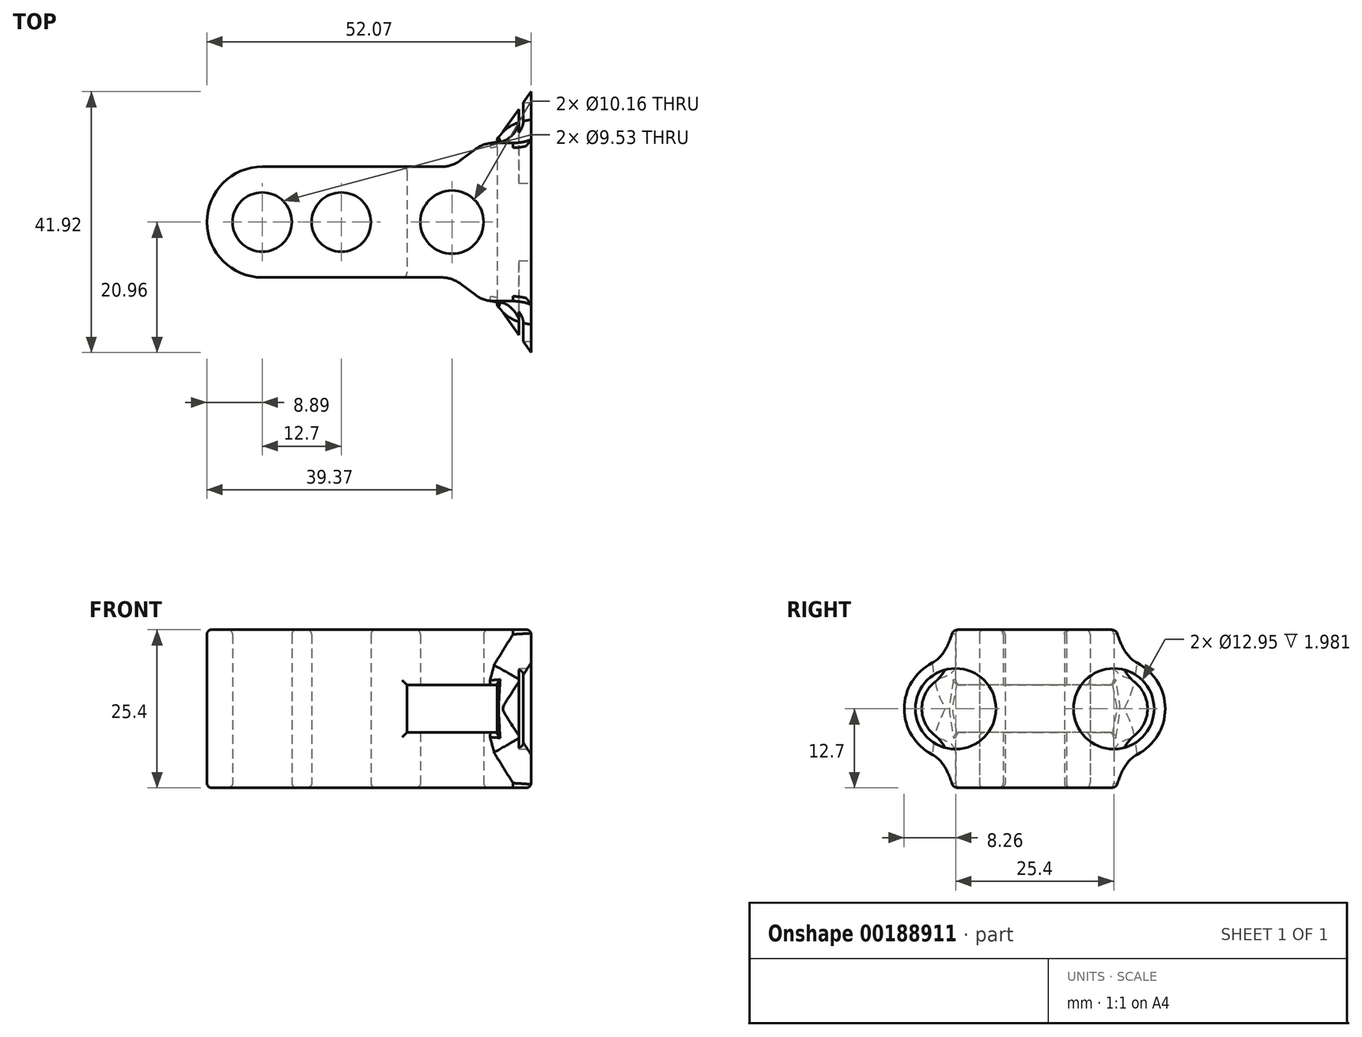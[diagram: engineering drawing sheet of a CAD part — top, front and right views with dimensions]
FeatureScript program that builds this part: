
annotation { "Feature Type Name" : "Feature", "Feature Type Description" : "" }
export const myFeature = defineFeature(function(context is Context, id is Id, definition is map)
    precondition{}
    {
        {
            var Q0;
            Q0=qCreatedBy(makeId("Top.planeOp"),FACE);
            var sketch = newSketch(context, id + "F0", { "sketchPlane" : qUnion([Q0])});
            skCircle(sketch, "E0", {"center": v(-12.7, 0) * mm, "radius": 4.76 * mm});
            skCircle(sketch, "E1", {"center": v(0, 0) * mm, "radius": 4.76 * mm});
            skCircle(sketch, "E2", {"center": v(17.78, 0) * mm, "radius": 5.08 * mm});
            skArc(sketch, "E3", {"start": v(-12.7, 8.9) * mm, "mid": v(-21.59, 0) * mm, "end": v(-12.7, -8.9) * mm});
            skLineSegment(sketch, "E4", {"start": v(-12.7, 8.9) * mm, "end": v(17.78, 8.9) * mm});
            skLineSegment(sketch, "E5", {"start": v(-12.7, 0) * mm, "end": v(-12.7, 8.9) * mm, "construction": true});
            skLineSegment(sketch, "E6", {"start": v(17.78, 0) * mm, "end": v(17.78, 8.9) * mm, "construction": true});
            skLineSegment(sketch, "E7", {"start": v(-12.7, -8.9) * mm, "end": v(17.78, -8.9) * mm});
            skLineSegment(sketch, "E8", {"start": v(30.48, 12.7) * mm, "end": v(30.48, -12.7) * mm});
            skLineSegment(sketch, "E9", {"start": v(30.48, -12.7) * mm, "end": v(22.86, -12.7) * mm});
            skLineSegment(sketch, "E10", {"start": v(22.86, -12.7) * mm, "end": v(17.78, -8.9) * mm});
            skLineSegment(sketch, "E11", {"start": v(30.48, 12.7) * mm, "end": v(22.86, 12.7) * mm});
            skLineSegment(sketch, "E12", {"start": v(22.86, 12.7) * mm, "end": v(17.78, 8.9) * mm});
            skLineSegment(sketch, "E13", {"start": v(17.78, 0) * mm, "end": v(30.48, 0) * mm, "construction": true});
            skLineSegment(sketch, "E14", {"start": v(17.78, 0) * mm, "end": v(17.78, -8.9) * mm, "construction": true});
            skSolve(sketch);
        }
        {
            var Q0;
            Q0=qSketchRegion(id+"F0",true);
            extrude(context, id + "F1", {"entities" : qUnion([Q0]), "depth" : 25.4 * mm});
        }
        {
            var Q0;
            Q0=qCreatedBy(makeId("Front.planeOp"),FACE);
            var sketch = newSketch(context, id + "F2", { "sketchPlane" : qUnion([Q0])});
            skLineSegment(sketch, "E15.bottom", {"start": v(10.54, 8.9) * mm, "end": v(25.02, 8.9) * mm});
            skLineSegment(sketch, "E15.top", {"start": v(10.54, 16.51) * mm, "end": v(25.02, 16.51) * mm});
            skLineSegment(sketch, "E15.left", {"start": v(10.54, 8.9) * mm, "end": v(10.54, 16.51) * mm});
            skLineSegment(sketch, "E15.right", {"start": v(25.02, 8.9) * mm, "end": v(25.02, 16.51) * mm});
            skLineSegment(sketch, "E16", {"start": v(10.54, 12.7) * mm, "end": v(0, 12.7) * mm, "construction": true});
            skLineSegment(sketch, "E17", {"start": v(17.78, 16.51) * mm, "end": v(17.78, 25.4) * mm, "construction": true});
            skSolve(sketch);
        }
        {
            var Q0;
            Q0=qSketchRegion(id+"F2",true);
            extrude(context, id + "F3", {"entities" : qUnion([Q0]), "operationType" : NewBodyOperationType.REMOVE, "endBound" : BoundingType.SYMMETRIC, "oppositeDirection" : true, "depth" : 25.4 * mm});
        }
        {
            var Q0;
            Q0=makeQuery(id+"F1.opExtrude","SWEPT_FACE",FACE,{"disambiguationData":[OSD([sQuery(id+"F0.wireOp",EDGE,"E8")])]});
            var sketch = newSketch(context, id + "F4", { "sketchPlane" : qUnion([Q0])});
            skCircle(sketch, "E18", {"center": v(-12.7, 12.7) * mm, "radius": 8.26 * mm});
            skCircle(sketch, "E19", {"center": v(12.7, 12.7) * mm, "radius": 8.26 * mm});
            skLineSegment(sketch, "E20", {"start": v(-12.7, 12.7) * mm, "end": v(0, 0) * mm, "construction": true});
            skLineSegment(sketch, "E21", {"start": v(0, 0) * mm, "end": v(12.7, 12.7) * mm, "construction": true});
            skLineSegment(sketch, "E22", {"start": v(-12.7, 12.7) * mm, "end": v(12.7, 12.7) * mm, "construction": true});
            skSolve(sketch);
        }
        {
            var Q0;
            Q0=qSketchRegion(id+"F4",true);
            extrude(context, id + "F5", {"entities" : qUnion([Q0]), "operationType" : NewBodyOperationType.ADD, "oppositeDirection" : true, "depth" : 5.46 * mm, "hasDraft" : true, "draftAngle" : 55 * degree, "draftPullDirection" : true});
        }
        {
            var Q0;
            {var subQ0=sQuery(id+"F0.wireOp",EDGE,"E12");var subQ1=sQuery(id+"F0.wireOp",EDGE,"E11");Q0=makeQuery(id+"F3.boolean.opBoolean","SPLIT",EDGE,{"disambiguationData":[TD([makeQuery(id+"F3.opExtrude","SWEPT_FACE",FACE,{"disambiguationData":[OSD([sQuery(id+"F2.wireOp",EDGE,"E15.bottom")])]})])],"derivedFrom":makeQuery(id+"F1.opExtrude","SWEPT_EDGE",EDGE,{"disambiguationData":[OSD([subQ1,subQ0])]})});}
            var Q1;
            {var subQ0=sQuery(id+"F0.wireOp",EDGE,"E12");var subQ1=sQuery(id+"F0.wireOp",EDGE,"E4");Q1=makeQuery(id+"F3.boolean.opBoolean","SPLIT",EDGE,{"disambiguationData":[TD([makeQuery(id+"F3.opExtrude","SWEPT_FACE",FACE,{"disambiguationData":[OSD([sQuery(id+"F2.wireOp",EDGE,"E15.bottom")])]})])],"derivedFrom":makeQuery(id+"F1.opExtrude","SWEPT_EDGE",EDGE,{"disambiguationData":[OSD([subQ1,subQ0])]})});}
            var Q2;
            {var subQ0=sQuery(id+"F0.wireOp",EDGE,"E12");var subQ1=sQuery(id+"F0.wireOp",EDGE,"E4");Q2=makeQuery(id+"F3.boolean.opBoolean","SPLIT",EDGE,{"disambiguationData":[TD([makeQuery(id+"F3.opExtrude","SWEPT_FACE",FACE,{"disambiguationData":[OSD([sQuery(id+"F2.wireOp",EDGE,"E15.top")])]})])],"derivedFrom":makeQuery(id+"F1.opExtrude","SWEPT_EDGE",EDGE,{"disambiguationData":[OSD([subQ1,subQ0])]})});}
            var Q3;
            {var subQ0=sQuery(id+"F0.wireOp",EDGE,"E12");var subQ1=sQuery(id+"F0.wireOp",EDGE,"E11");Q3=makeQuery(id+"F3.boolean.opBoolean","SPLIT",EDGE,{"disambiguationData":[TD([makeQuery(id+"F3.opExtrude","SWEPT_FACE",FACE,{"disambiguationData":[OSD([sQuery(id+"F2.wireOp",EDGE,"E15.top")])]})])],"derivedFrom":makeQuery(id+"F1.opExtrude","SWEPT_EDGE",EDGE,{"disambiguationData":[OSD([subQ1,subQ0])]})});}
            var Q4;
            {var subQ0=sQuery(id+"F0.wireOp",EDGE,"E10");var subQ1=sQuery(id+"F0.wireOp",EDGE,"E7");Q4=makeQuery(id+"F3.boolean.opBoolean","SPLIT",EDGE,{"disambiguationData":[TD([makeQuery(id+"F3.opExtrude","SWEPT_FACE",FACE,{"disambiguationData":[OSD([sQuery(id+"F2.wireOp",EDGE,"E15.top")])]})])],"derivedFrom":makeQuery(id+"F1.opExtrude","SWEPT_EDGE",EDGE,{"disambiguationData":[OSD([subQ1,subQ0])]})});}
            var Q5;
            {var subQ0=sQuery(id+"F0.wireOp",EDGE,"E10");var subQ1=sQuery(id+"F0.wireOp",EDGE,"E9");Q5=makeQuery(id+"F3.boolean.opBoolean","SPLIT",EDGE,{"disambiguationData":[TD([makeQuery(id+"F3.opExtrude","SWEPT_FACE",FACE,{"disambiguationData":[OSD([sQuery(id+"F2.wireOp",EDGE,"E15.top")])]})])],"derivedFrom":makeQuery(id+"F1.opExtrude","SWEPT_EDGE",EDGE,{"disambiguationData":[OSD([subQ1,subQ0])]})});}
            var Q6;
            {var subQ0=sQuery(id+"F0.wireOp",EDGE,"E10");var subQ1=sQuery(id+"F0.wireOp",EDGE,"E7");Q6=makeQuery(id+"F3.boolean.opBoolean","SPLIT",EDGE,{"disambiguationData":[TD([makeQuery(id+"F3.opExtrude","SWEPT_FACE",FACE,{"disambiguationData":[OSD([sQuery(id+"F2.wireOp",EDGE,"E15.bottom")])]})])],"derivedFrom":makeQuery(id+"F1.opExtrude","SWEPT_EDGE",EDGE,{"disambiguationData":[OSD([subQ1,subQ0])]})});}
            var Q7;
            {var subQ0=sQuery(id+"F0.wireOp",EDGE,"E10");var subQ1=sQuery(id+"F0.wireOp",EDGE,"E9");Q7=makeQuery(id+"F3.boolean.opBoolean","SPLIT",EDGE,{"disambiguationData":[TD([makeQuery(id+"F3.opExtrude","SWEPT_FACE",FACE,{"disambiguationData":[OSD([sQuery(id+"F2.wireOp",EDGE,"E15.bottom")])]})])],"derivedFrom":makeQuery(id+"F1.opExtrude","SWEPT_EDGE",EDGE,{"disambiguationData":[OSD([subQ1,subQ0])]})});}
            fillet(context, id + "F6", {"entities" : qUnion([Q0, Q1, Q2, Q3, Q4, Q5, Q6, Q7]), "radius" : 5.08 * mm, "tangentPropagation" : true, "allowEdgeOverflow" : false});
        }
        {
            var Q0;
            Q0=makeQuery(id+"F5.boolean.opBoolean","INTERSECT",EDGE,{"disambiguationData":[OD(0.0)],"derivedFrom":[makeQuery(id+"F1.opExtrude","SWEPT_FACE",FACE,{"disambiguationData":[OSD([sQuery(id+"F0.wireOp",EDGE,"E9")])]}),makeQuery(id+"F5.opExtrude","SWEPT_FACE",FACE,{"disambiguationData":[OSD([sQuery(id+"F4.wireOp",EDGE,"E18")])]})]});
            var Q1;
            Q1=makeQuery(id+"F5.boolean.opBoolean","INTERSECT",EDGE,{"disambiguationData":[OD(1.0)],"derivedFrom":[makeQuery(id+"F1.opExtrude","SWEPT_FACE",FACE,{"disambiguationData":[OSD([sQuery(id+"F0.wireOp",EDGE,"E9")])]}),makeQuery(id+"F5.opExtrude","SWEPT_FACE",FACE,{"disambiguationData":[OSD([sQuery(id+"F4.wireOp",EDGE,"E18")])]})]});
            var Q2;
            Q2=makeQuery(id+"F5.boolean.opBoolean","INTERSECT",EDGE,{"disambiguationData":[OD(1.0)],"derivedFrom":[makeQuery(id+"F1.opExtrude","SWEPT_FACE",FACE,{"disambiguationData":[OSD([sQuery(id+"F0.wireOp",EDGE,"E11")])]}),makeQuery(id+"F5.opExtrude","SWEPT_FACE",FACE,{"disambiguationData":[OSD([sQuery(id+"F4.wireOp",EDGE,"E19")])]})]});
            var Q3;
            Q3=makeQuery(id+"F5.boolean.opBoolean","INTERSECT",EDGE,{"disambiguationData":[OD(0.0)],"derivedFrom":[makeQuery(id+"F1.opExtrude","SWEPT_FACE",FACE,{"disambiguationData":[OSD([sQuery(id+"F0.wireOp",EDGE,"E11")])]}),makeQuery(id+"F5.opExtrude","SWEPT_FACE",FACE,{"disambiguationData":[OSD([sQuery(id+"F4.wireOp",EDGE,"E19")])]})]});
            fillet(context, id + "F7", {"entities" : qUnion([Q0, Q1, Q2, Q3]), "radius" : 5.08 * mm, "tangentPropagation" : true, "allowEdgeOverflow" : false});
        }
        {
            var Q0;
            {var subQ0=sQuery(id+"F4.wireOp",EDGE,"E18");Q0=makeQuery(id+"F7.opFillet","BLEND_EDGE",EDGE,{"disambiguationData":[OD(1.0)],"blendedFrom":[makeQuery(id+"F5.boolean.opBoolean","INTERSECT",EDGE,{"disambiguationData":[OD(1.0)],"derivedFrom":[makeQuery(id+"F1.opExtrude","SWEPT_FACE",FACE,{"disambiguationData":[OSD([sQuery(id+"F0.wireOp",EDGE,"E9")])]}),makeQuery(id+"F5.opExtrude","SWEPT_FACE",FACE,{"disambiguationData":[OSD([subQ0])]})]}),makeQuery(id+"F5.boolean.opBoolean","MERGE",FACE,{"derivedFrom":[makeQuery(id+"F3.boolean.opBoolean","COPY",FACE,{"derivedFrom":makeQuery(id+"F3.opExtrude","SWEPT_FACE",FACE,{"disambiguationData":[OSD([sQuery(id+"F2.wireOp",EDGE,"E15.right")])]})}),makeQuery(id+"F5.opExtrude","CAP_FACE",FACE,{"disambiguationData":[OSD([subQ0])],"isStart":false}),makeQuery(id+"F5.opExtrude","CAP_FACE",FACE,{"disambiguationData":[OSD([sQuery(id+"F4.wireOp",EDGE,"E19")])],"isStart":false})]})],"blendedInto":[makeQuery(id+"F5.boolean.opBoolean","MERGE",FACE,{"derivedFrom":[makeQuery(id+"F3.boolean.opBoolean","COPY",FACE,{"derivedFrom":makeQuery(id+"F3.opExtrude","SWEPT_FACE",FACE,{"disambiguationData":[OSD([sQuery(id+"F2.wireOp",EDGE,"E15.right")])]})}),makeQuery(id+"F5.opExtrude","CAP_FACE",FACE,{"disambiguationData":[OSD([subQ0])],"isStart":false}),makeQuery(id+"F5.opExtrude","CAP_FACE",FACE,{"disambiguationData":[OSD([sQuery(id+"F4.wireOp",EDGE,"E19")])],"isStart":false})]})]});}
            var Q1;
            Q1=makeQuery(id+"F5.opExtrude","CAP_EDGE",EDGE,{"disambiguationData":[OSD([sQuery(id+"F4.wireOp",EDGE,"E18")])],"isStart":false});
            var Q2;
            {var subQ0=sQuery(id+"F4.wireOp",EDGE,"E18");Q2=makeQuery(id+"F7.opFillet","BLEND_EDGE",EDGE,{"disambiguationData":[OD(1.0)],"blendedFrom":[makeQuery(id+"F5.boolean.opBoolean","INTERSECT",EDGE,{"disambiguationData":[OD(0.0)],"derivedFrom":[makeQuery(id+"F1.opExtrude","SWEPT_FACE",FACE,{"disambiguationData":[OSD([sQuery(id+"F0.wireOp",EDGE,"E9")])]}),makeQuery(id+"F5.opExtrude","SWEPT_FACE",FACE,{"disambiguationData":[OSD([subQ0])]})]}),makeQuery(id+"F5.boolean.opBoolean","MERGE",FACE,{"derivedFrom":[makeQuery(id+"F3.boolean.opBoolean","COPY",FACE,{"derivedFrom":makeQuery(id+"F3.opExtrude","SWEPT_FACE",FACE,{"disambiguationData":[OSD([sQuery(id+"F2.wireOp",EDGE,"E15.right")])]})}),makeQuery(id+"F5.opExtrude","CAP_FACE",FACE,{"disambiguationData":[OSD([subQ0])],"isStart":false}),makeQuery(id+"F5.opExtrude","CAP_FACE",FACE,{"disambiguationData":[OSD([sQuery(id+"F4.wireOp",EDGE,"E19")])],"isStart":false})]})],"blendedInto":[makeQuery(id+"F5.boolean.opBoolean","MERGE",FACE,{"derivedFrom":[makeQuery(id+"F3.boolean.opBoolean","COPY",FACE,{"derivedFrom":makeQuery(id+"F3.opExtrude","SWEPT_FACE",FACE,{"disambiguationData":[OSD([sQuery(id+"F2.wireOp",EDGE,"E15.right")])]})}),makeQuery(id+"F5.opExtrude","CAP_FACE",FACE,{"disambiguationData":[OSD([subQ0])],"isStart":false}),makeQuery(id+"F5.opExtrude","CAP_FACE",FACE,{"disambiguationData":[OSD([sQuery(id+"F4.wireOp",EDGE,"E19")])],"isStart":false})]})]});}
            var Q3;
            Q3=makeQuery(id+"F3.boolean.opBoolean","INTERSECT",EDGE,{"derivedFrom":[makeQuery(id+"F1.opExtrude","SWEPT_FACE",FACE,{"disambiguationData":[OSD([sQuery(id+"F0.wireOp",EDGE,"E10")])]}),makeQuery(id+"F3.opExtrude","SWEPT_FACE",FACE,{"disambiguationData":[OSD([sQuery(id+"F2.wireOp",EDGE,"E15.top")])]})]});
            var Q4;
            Q4=makeQuery(id+"F3.boolean.opBoolean","INTERSECT",EDGE,{"derivedFrom":[makeQuery(id+"F1.opExtrude","SWEPT_FACE",FACE,{"disambiguationData":[OSD([sQuery(id+"F0.wireOp",EDGE,"E7")])]}),makeQuery(id+"F3.opExtrude","SWEPT_FACE",FACE,{"disambiguationData":[OSD([sQuery(id+"F2.wireOp",EDGE,"E15.top")])]})]});
            var Q5;
            Q5=makeQuery(id+"F3.boolean.opBoolean","INTERSECT",EDGE,{"derivedFrom":[makeQuery(id+"F1.opExtrude","SWEPT_FACE",FACE,{"disambiguationData":[OSD([sQuery(id+"F0.wireOp",EDGE,"E7")])]}),makeQuery(id+"F3.opExtrude","SWEPT_FACE",FACE,{"disambiguationData":[OSD([sQuery(id+"F2.wireOp",EDGE,"E15.left")])]})]});
            var Q6;
            Q6=makeQuery(id+"F3.boolean.opBoolean","INTERSECT",EDGE,{"derivedFrom":[makeQuery(id+"F1.opExtrude","SWEPT_FACE",FACE,{"disambiguationData":[OSD([sQuery(id+"F0.wireOp",EDGE,"E7")])]}),makeQuery(id+"F3.opExtrude","SWEPT_FACE",FACE,{"disambiguationData":[OSD([sQuery(id+"F2.wireOp",EDGE,"E15.bottom")])]})]});
            var Q7;
            Q7=makeQuery(id+"F3.boolean.opBoolean","INTERSECT",EDGE,{"derivedFrom":[makeQuery(id+"F1.opExtrude","SWEPT_FACE",FACE,{"disambiguationData":[OSD([sQuery(id+"F0.wireOp",EDGE,"E10")])]}),makeQuery(id+"F3.opExtrude","SWEPT_FACE",FACE,{"disambiguationData":[OSD([sQuery(id+"F2.wireOp",EDGE,"E15.bottom")])]})]});
            var Q8;
            Q8=makeQuery(id+"F7.opFillet","BLEND_EDGE",EDGE,{"disambiguationData":[OD(0.0)],"blendedFrom":[makeQuery(id+"F5.boolean.opBoolean","INTERSECT",EDGE,{"disambiguationData":[OD(0.0)],"derivedFrom":[makeQuery(id+"F1.opExtrude","SWEPT_FACE",FACE,{"disambiguationData":[OSD([sQuery(id+"F0.wireOp",EDGE,"E9")])]}),makeQuery(id+"F5.opExtrude","SWEPT_FACE",FACE,{"disambiguationData":[OSD([sQuery(id+"F4.wireOp",EDGE,"E18")])]})]}),makeQuery(id+"F3.boolean.opBoolean","COPY",FACE,{"derivedFrom":makeQuery(id+"F3.opExtrude","SWEPT_FACE",FACE,{"disambiguationData":[OSD([sQuery(id+"F2.wireOp",EDGE,"E15.bottom")])]})})],"blendedInto":[makeQuery(id+"F3.boolean.opBoolean","COPY",FACE,{"derivedFrom":makeQuery(id+"F3.opExtrude","SWEPT_FACE",FACE,{"disambiguationData":[OSD([sQuery(id+"F2.wireOp",EDGE,"E15.bottom")])]})})]});
            var Q9;
            {var subQ0=sQuery(id+"F4.wireOp",EDGE,"E19");Q9=makeQuery(id+"F7.opFillet","BLEND_EDGE",EDGE,{"disambiguationData":[OD(1.0)],"blendedFrom":[makeQuery(id+"F5.boolean.opBoolean","INTERSECT",EDGE,{"disambiguationData":[OD(1.0)],"derivedFrom":[makeQuery(id+"F1.opExtrude","SWEPT_FACE",FACE,{"disambiguationData":[OSD([sQuery(id+"F0.wireOp",EDGE,"E11")])]}),makeQuery(id+"F5.opExtrude","SWEPT_FACE",FACE,{"disambiguationData":[OSD([subQ0])]})]}),makeQuery(id+"F5.boolean.opBoolean","MERGE",FACE,{"derivedFrom":[makeQuery(id+"F3.boolean.opBoolean","COPY",FACE,{"derivedFrom":makeQuery(id+"F3.opExtrude","SWEPT_FACE",FACE,{"disambiguationData":[OSD([sQuery(id+"F2.wireOp",EDGE,"E15.right")])]})}),makeQuery(id+"F5.opExtrude","CAP_FACE",FACE,{"disambiguationData":[OSD([sQuery(id+"F4.wireOp",EDGE,"E18")])],"isStart":false}),makeQuery(id+"F5.opExtrude","CAP_FACE",FACE,{"disambiguationData":[OSD([subQ0])],"isStart":false})]})],"blendedInto":[makeQuery(id+"F5.boolean.opBoolean","MERGE",FACE,{"derivedFrom":[makeQuery(id+"F3.boolean.opBoolean","COPY",FACE,{"derivedFrom":makeQuery(id+"F3.opExtrude","SWEPT_FACE",FACE,{"disambiguationData":[OSD([sQuery(id+"F2.wireOp",EDGE,"E15.right")])]})}),makeQuery(id+"F5.opExtrude","CAP_FACE",FACE,{"disambiguationData":[OSD([sQuery(id+"F4.wireOp",EDGE,"E18")])],"isStart":false}),makeQuery(id+"F5.opExtrude","CAP_FACE",FACE,{"disambiguationData":[OSD([subQ0])],"isStart":false})]})]});}
            var Q10;
            Q10=makeQuery(id+"F7.opFillet","BLEND_EDGE",EDGE,{"disambiguationData":[OD(0.0)],"blendedFrom":[makeQuery(id+"F5.boolean.opBoolean","INTERSECT",EDGE,{"disambiguationData":[OD(1.0)],"derivedFrom":[makeQuery(id+"F1.opExtrude","SWEPT_FACE",FACE,{"disambiguationData":[OSD([sQuery(id+"F0.wireOp",EDGE,"E11")])]}),makeQuery(id+"F5.opExtrude","SWEPT_FACE",FACE,{"disambiguationData":[OSD([sQuery(id+"F4.wireOp",EDGE,"E19")])]})]}),makeQuery(id+"F3.boolean.opBoolean","COPY",FACE,{"derivedFrom":makeQuery(id+"F3.opExtrude","SWEPT_FACE",FACE,{"disambiguationData":[OSD([sQuery(id+"F2.wireOp",EDGE,"E15.top")])]})})],"blendedInto":[makeQuery(id+"F3.boolean.opBoolean","COPY",FACE,{"derivedFrom":makeQuery(id+"F3.opExtrude","SWEPT_FACE",FACE,{"disambiguationData":[OSD([sQuery(id+"F2.wireOp",EDGE,"E15.top")])]})})]});
            var Q11;
            Q11=makeQuery(id+"F3.boolean.opBoolean","INTERSECT",EDGE,{"derivedFrom":[makeQuery(id+"F1.opExtrude","SWEPT_FACE",FACE,{"disambiguationData":[OSD([sQuery(id+"F0.wireOp",EDGE,"E12")])]}),makeQuery(id+"F3.opExtrude","SWEPT_FACE",FACE,{"disambiguationData":[OSD([sQuery(id+"F2.wireOp",EDGE,"E15.top")])]})]});
            var Q12;
            Q12=makeQuery(id+"F3.boolean.opBoolean","INTERSECT",EDGE,{"derivedFrom":[makeQuery(id+"F1.opExtrude","SWEPT_FACE",FACE,{"disambiguationData":[OSD([sQuery(id+"F0.wireOp",EDGE,"E4")])]}),makeQuery(id+"F3.opExtrude","SWEPT_FACE",FACE,{"disambiguationData":[OSD([sQuery(id+"F2.wireOp",EDGE,"E15.top")])]})]});
            var Q13;
            Q13=makeQuery(id+"F3.boolean.opBoolean","INTERSECT",EDGE,{"derivedFrom":[makeQuery(id+"F1.opExtrude","SWEPT_FACE",FACE,{"disambiguationData":[OSD([sQuery(id+"F0.wireOp",EDGE,"E4")])]}),makeQuery(id+"F3.opExtrude","SWEPT_FACE",FACE,{"disambiguationData":[OSD([sQuery(id+"F2.wireOp",EDGE,"E15.left")])]})]});
            var Q14;
            Q14=makeQuery(id+"F3.boolean.opBoolean","INTERSECT",EDGE,{"derivedFrom":[makeQuery(id+"F1.opExtrude","SWEPT_FACE",FACE,{"disambiguationData":[OSD([sQuery(id+"F0.wireOp",EDGE,"E4")])]}),makeQuery(id+"F3.opExtrude","SWEPT_FACE",FACE,{"disambiguationData":[OSD([sQuery(id+"F2.wireOp",EDGE,"E15.bottom")])]})]});
            var Q15;
            Q15=makeQuery(id+"F3.boolean.opBoolean","INTERSECT",EDGE,{"derivedFrom":[makeQuery(id+"F1.opExtrude","SWEPT_FACE",FACE,{"disambiguationData":[OSD([sQuery(id+"F0.wireOp",EDGE,"E12")])]}),makeQuery(id+"F3.opExtrude","SWEPT_FACE",FACE,{"disambiguationData":[OSD([sQuery(id+"F2.wireOp",EDGE,"E15.bottom")])]})]});
            var Q16;
            Q16=makeQuery(id+"F7.opFillet","BLEND_EDGE",EDGE,{"disambiguationData":[OD(0.0)],"blendedFrom":[makeQuery(id+"F5.boolean.opBoolean","INTERSECT",EDGE,{"disambiguationData":[OD(0.0)],"derivedFrom":[makeQuery(id+"F1.opExtrude","SWEPT_FACE",FACE,{"disambiguationData":[OSD([sQuery(id+"F0.wireOp",EDGE,"E11")])]}),makeQuery(id+"F5.opExtrude","SWEPT_FACE",FACE,{"disambiguationData":[OSD([sQuery(id+"F4.wireOp",EDGE,"E19")])]})]}),makeQuery(id+"F3.boolean.opBoolean","COPY",FACE,{"derivedFrom":makeQuery(id+"F3.opExtrude","SWEPT_FACE",FACE,{"disambiguationData":[OSD([sQuery(id+"F2.wireOp",EDGE,"E15.bottom")])]})})],"blendedInto":[makeQuery(id+"F3.boolean.opBoolean","COPY",FACE,{"derivedFrom":makeQuery(id+"F3.opExtrude","SWEPT_FACE",FACE,{"disambiguationData":[OSD([sQuery(id+"F2.wireOp",EDGE,"E15.bottom")])]})})]});
            fillet(context, id + "F8", {"entities" : qUnion([Q0, Q1, Q2, Q3, Q4, Q5, Q6, Q7, Q8, Q9, Q10, Q11, Q12, Q13, Q14, Q15, Q16]), "radius" : 0.76 * mm, "tangentPropagation" : true, "allowEdgeOverflow" : false});
        }
        {
            var Q0;
            Q0=makeQuery(id+"F5.boolean.opBoolean","MERGE",FACE,{"derivedFrom":[makeQuery(id+"F1.opExtrude","SWEPT_FACE",FACE,{"disambiguationData":[OSD([sQuery(id+"F0.wireOp",EDGE,"E8")])]}),makeQuery(id+"F5.opExtrude","CAP_FACE",FACE,{"disambiguationData":[OSD([sQuery(id+"F4.wireOp",EDGE,"E18")])],"isStart":true}),makeQuery(id+"F5.opExtrude","CAP_FACE",FACE,{"disambiguationData":[OSD([sQuery(id+"F4.wireOp",EDGE,"E19")])],"isStart":true})]});
            var sketch = newSketch(context, id + "F9", { "sketchPlane" : qUnion([Q0])});
            skCircle(sketch, "E23", {"center": v(-12.7, 12.7) * mm, "radius": 6.48 * mm});
            skCircle(sketch, "E24", {"center": v(12.7, 12.7) * mm, "radius": 6.48 * mm});
            skSolve(sketch);
        }
        {
            var Q0;
            Q0=qSketchRegion(id+"F9",true);
            extrude(context, id + "F10", {"entities" : qUnion([Q0]), "operationType" : NewBodyOperationType.REMOVE, "oppositeDirection" : true, "depth" : 1.98 * mm});
        }
        {
            var Q0;
            Q0=makeQuery(id+"F1.opExtrude","CAP_FACE",FACE,{"disambiguationData":[OSD([sQuery(id+"F0.wireOp",EDGE,"E0"),sQuery(id+"F0.wireOp",EDGE,"E1"),sQuery(id+"F0.wireOp",EDGE,"E2"),sQuery(id+"F0.wireOp",EDGE,"E3"),sQuery(id+"F0.wireOp",EDGE,"E4"),sQuery(id+"F0.wireOp",EDGE,"E7"),sQuery(id+"F0.wireOp",EDGE,"E8"),sQuery(id+"F0.wireOp",EDGE,"E9"),sQuery(id+"F0.wireOp",EDGE,"E10"),sQuery(id+"F0.wireOp",EDGE,"E11"),sQuery(id+"F0.wireOp",EDGE,"E12")])],"isStart":false});
            var Q1;
            Q1=makeQuery(id+"F1.opExtrude","CAP_FACE",FACE,{"disambiguationData":[OSD([sQuery(id+"F0.wireOp",EDGE,"E0"),sQuery(id+"F0.wireOp",EDGE,"E1"),sQuery(id+"F0.wireOp",EDGE,"E2"),sQuery(id+"F0.wireOp",EDGE,"E3"),sQuery(id+"F0.wireOp",EDGE,"E4"),sQuery(id+"F0.wireOp",EDGE,"E7"),sQuery(id+"F0.wireOp",EDGE,"E8"),sQuery(id+"F0.wireOp",EDGE,"E9"),sQuery(id+"F0.wireOp",EDGE,"E10"),sQuery(id+"F0.wireOp",EDGE,"E11"),sQuery(id+"F0.wireOp",EDGE,"E12")])],"isStart":true});
            fillet(context, id + "F11", {"entities" : qUnion([Q0, Q1]), "radius" : 0.76 * mm, "tangentPropagation" : true, "allowEdgeOverflow" : false});
        }
    });
